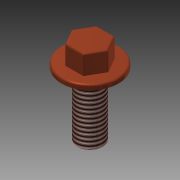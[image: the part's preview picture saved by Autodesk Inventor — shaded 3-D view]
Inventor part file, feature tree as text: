
AUTODESK INVENTOR PART (.ipt)
format: ipt  version: 2015 (Build 190159000, 159)  size: 133,632 bytes
history: native  units: mm
features: extrude x3, sketch x3, fillet x1, thread x1, chamfer x1
ambient origin geometry x8: Origin, YZ Plane, XZ Plane, XY Plane, X Axis, Y Axis, Z Axis, Center Point
bodies: 实体1 (feature_tree)
feature tree (9):
  extrude  "拉伸1"  Depth=1.5mm TaperAngle=0.0deg
  extrude  "拉伸2"  Depth=10.0mm
  fillet  "圆角1"  Radius=6.0mm
  extrude  "拉伸3"  Depth=10.0mm
  thread  "螺纹1"  [1 undecoded]
  chamfer  "倒角1"  Distance=10.0mm
  sketch  "草图1"  dims[d0=18.0mm d1=1.5mm d2=0.0mm]
  sketch  "草图2"  dims[d3=3.053728mm d4=10.0mm d5=6.0mm d6=0.0mm]
  sketch  "草图3"  dims[d7=0.5mm d8=8.0mm d9=20.0mm d10=0.0mm d11=10.0mm d12=0.0mm d13=0.25mm d14=2.0mm d15=45.0deg]
note: 1 required parameter value undecoded (feature->parameter linkage not recoverable at this tier; creation-order binding heuristic only, values carry confidence <= 0.55)
